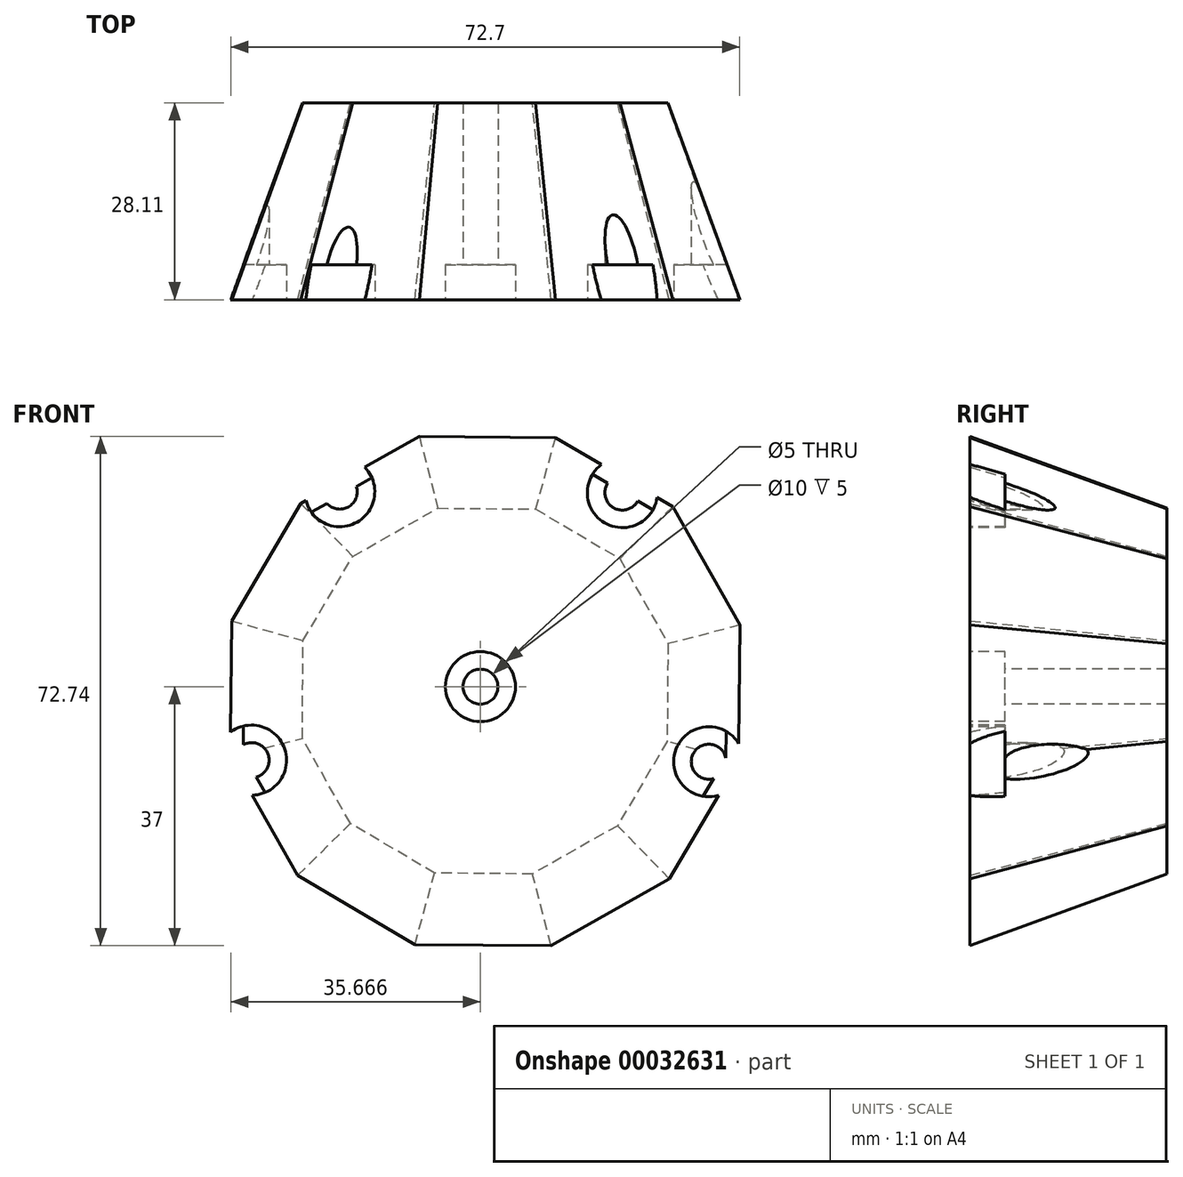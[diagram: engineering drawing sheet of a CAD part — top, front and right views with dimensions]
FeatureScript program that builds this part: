
annotation { "Feature Type Name" : "Feature", "Feature Type Description" : "" }
export const myFeature = defineFeature(function(context is Context, id is Id, definition is map)
    precondition{}
    {
        {
            var Q0;
            Q0=qCreatedBy(makeId("Front.planeOp"),FACE);
            var sketch = newSketch(context, id + "F0", { "sketchPlane" : qUnion([Q0])});
            skCircle(sketch, "E0.cCircle", {"center": v(-44.38, 27.24) * mm, "radius": 26.05 * mm, "construction": true});
            skLineSegment(sketch, "E0.0", {"start": v(-25.48, 8) * mm, "end": v(-37.63, 1.13) * mm});
            skLineSegment(sketch, "E0.1", {"start": v(-37.63, 1.13) * mm, "end": v(-51.6, 1.25) * mm});
            skLineSegment(sketch, "E0.2", {"start": v(-51.6, 1.25) * mm, "end": v(-63.62, 8.33) * mm});
            skLineSegment(sketch, "E0.3", {"start": v(-63.62, 8.33) * mm, "end": v(-70.5, 20.48) * mm});
            skLineSegment(sketch, "E0.4", {"start": v(-70.5, 20.48) * mm, "end": v(-70.38, 34.45) * mm});
            skLineSegment(sketch, "E0.5", {"start": v(-70.38, 34.45) * mm, "end": v(-63.3, 46.48) * mm});
            skLineSegment(sketch, "E0.6", {"start": v(-63.3, 46.48) * mm, "end": v(-51.14, 53.35) * mm});
            skLineSegment(sketch, "E0.7", {"start": v(-51.14, 53.35) * mm, "end": v(-37.18, 53.23) * mm});
            skLineSegment(sketch, "E0.8", {"start": v(-37.18, 53.23) * mm, "end": v(-25.15, 46.15) * mm});
            skLineSegment(sketch, "E0.9", {"start": v(-25.15, 46.15) * mm, "end": v(-18.27, 34) * mm});
            skLineSegment(sketch, "E0.10", {"start": v(-18.27, 34) * mm, "end": v(-18.4, 20.03) * mm});
            skLineSegment(sketch, "E0.11", {"start": v(-18.4, 20.03) * mm, "end": v(-25.48, 8) * mm});
            skPoint(sketch, "E0.0.midPoint", {"position": v(-31.55, 4.56) * mm});
            skSolve(sketch);
        }
        {
            var Q0;
            Q0 = qSketchRegion(id + "F0", true);
            extrude(context, id + "F1", {"entities" : qUnion([Q0]), "depth" : 28.1 * mm, "hasDraft" : true, "draftAngle" : 20 * degree});
        }
        {
            var Q0;
            Q0=makeQuery(id+"F1.opExtrude","CAP_FACE",FACE,{"disambiguationData":[OSD([sQuery(id+"F0.wireOp",EDGE,"E0.0"),sQuery(id+"F0.wireOp",EDGE,"E0.1"),sQuery(id+"F0.wireOp",EDGE,"E0.2"),sQuery(id+"F0.wireOp",EDGE,"E0.3"),sQuery(id+"F0.wireOp",EDGE,"E0.4"),sQuery(id+"F0.wireOp",EDGE,"E0.5"),sQuery(id+"F0.wireOp",EDGE,"E0.6"),sQuery(id+"F0.wireOp",EDGE,"E0.7"),sQuery(id+"F0.wireOp",EDGE,"E0.8"),sQuery(id+"F0.wireOp",EDGE,"E0.9"),sQuery(id+"F0.wireOp",EDGE,"E0.10"),sQuery(id+"F0.wireOp",EDGE,"E0.11")])],"isStart":false});
            var sketch = newSketch(context, id + "F2", { "sketchPlane" : qUnion([Q0])});
            skCircle(sketch, "E1.cCircle", {"center": v(-45.05, 27.87) * mm, "radius": 27.77 * mm, "construction": true});
            skLineSegment(sketch, "E1.0", {"start": v(-12.44, 17.15) * mm, "end": v(-45.17, -6.46) * mm});
            skLineSegment(sketch, "E1.1", {"start": v(-45.17, -6.46) * mm, "end": v(-77.74, 17.37) * mm});
            skLineSegment(sketch, "E1.2", {"start": v(-77.74, 17.37) * mm, "end": v(-65.14, 55.71) * mm});
            skLineSegment(sketch, "E1.3", {"start": v(-65.14, 55.71) * mm, "end": v(-24.78, 55.58) * mm});
            skLineSegment(sketch, "E1.4", {"start": v(-24.78, 55.58) * mm, "end": v(-12.44, 17.15) * mm});
            skPoint(sketch, "E1.0.midPoint", {"position": v(-28.8, 5.35) * mm});
            skSolve(sketch);
        }
        {
            var Q0;
            Q0=sQuery(id+"F2.wireOp",VERTEX,"E1.2.start");
            var Q1;
            Q1=sQuery(id+"F2.wireOp",VERTEX,"E1.3.start");
            var Q2;
            Q2=sQuery(id+"F2.wireOp",VERTEX,"E1.4.start");
            var Q3;
            Q3=sQuery(id+"F2.wireOp",VERTEX,"E1.4.end");
            var Q4;
            Q4=sQuery(id+"F2.wireOp",VERTEX,"E1.cCircle.center");
            var Q5;
            Q5=makeQuery(id+"F1.opExtrude","SWEPT_BODY",BODY,{"disambiguationData":[OSD([sQuery(id+"F0.wireOp",EDGE,"E0.0"),sQuery(id+"F0.wireOp",EDGE,"E0.1"),sQuery(id+"F0.wireOp",EDGE,"E0.2"),sQuery(id+"F0.wireOp",EDGE,"E0.3"),sQuery(id+"F0.wireOp",EDGE,"E0.4"),sQuery(id+"F0.wireOp",EDGE,"E0.5"),sQuery(id+"F0.wireOp",EDGE,"E0.6"),sQuery(id+"F0.wireOp",EDGE,"E0.7"),sQuery(id+"F0.wireOp",EDGE,"E0.8"),sQuery(id+"F0.wireOp",EDGE,"E0.9"),sQuery(id+"F0.wireOp",EDGE,"E0.10"),sQuery(id+"F0.wireOp",EDGE,"E0.11")])]});
            hole(context, id + "F3", {"style" : HoleStyle.C_BORE, "holeDiameter" : 5 * mm, "cBoreDiameter" : 10 * mm, "cBoreDepth" : 5 * mm, "endStyle" : HoleEndStyle.THROUGH, "locations" : qUnion([Q0, Q1, Q2, Q3, Q4]), "scope" : qUnion([Q5])});
        }
    });
